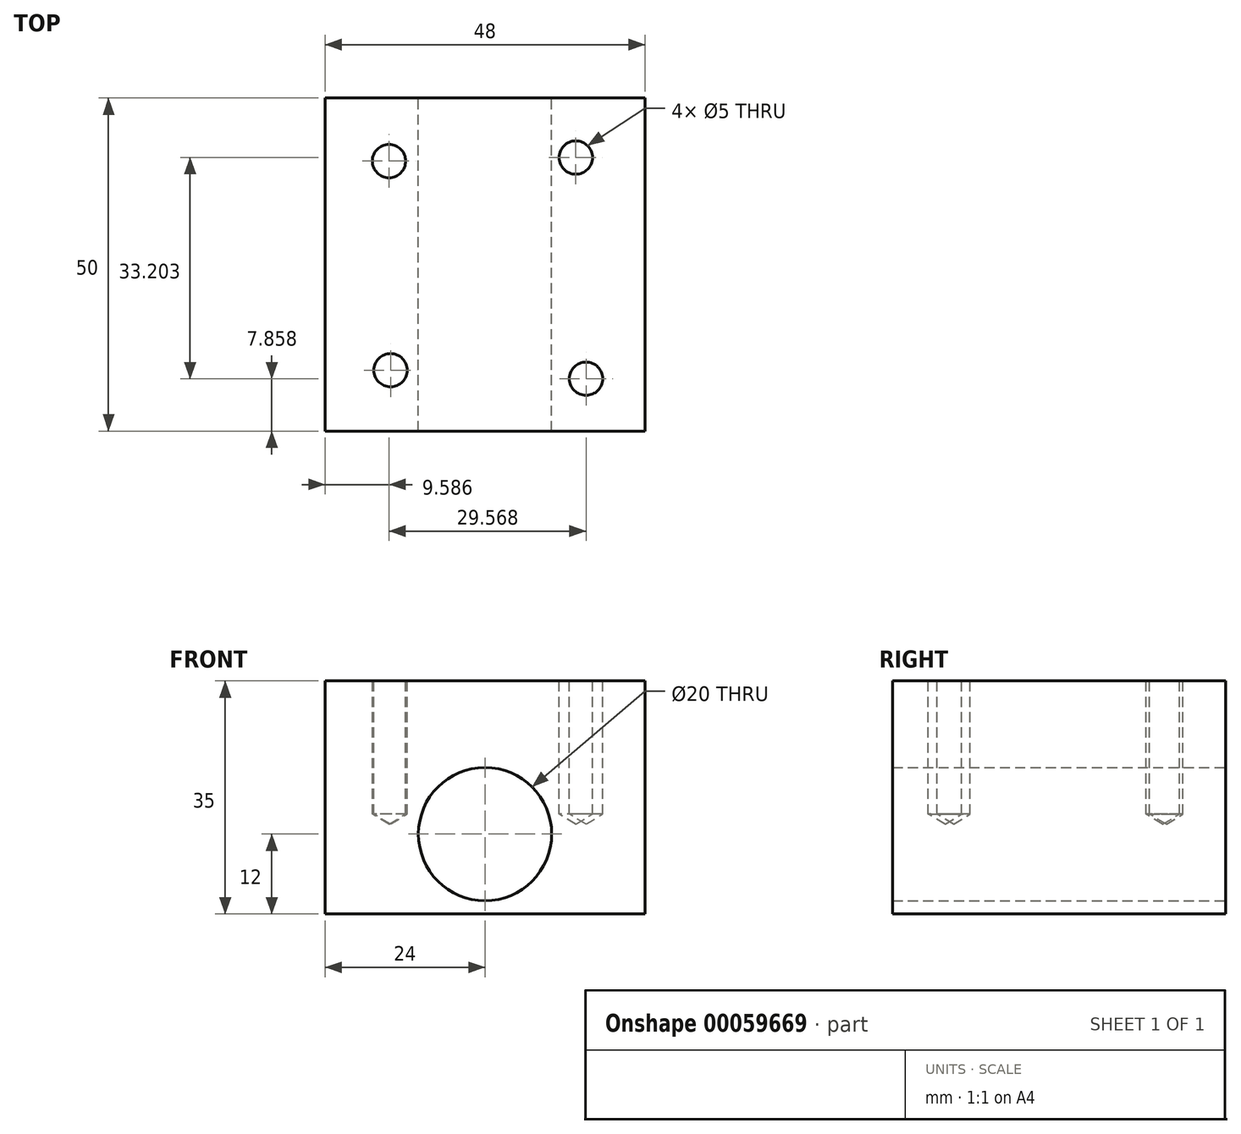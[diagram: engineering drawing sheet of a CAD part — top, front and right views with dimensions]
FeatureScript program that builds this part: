
annotation { "Feature Type Name" : "Feature", "Feature Type Description" : "" }
export const myFeature = defineFeature(function(context is Context, id is Id, definition is map)
    precondition{}
    {
        {
            var Q0;
            Q0=qCreatedBy(makeId("Front.planeOp"),FACE);
            var sketch = newSketch(context, id + "F0", { "sketchPlane" : qUnion([Q0])});
            skLineSegment(sketch, "E0.rect.bottom", {"start": v(24, 17.5) * mm, "end": v(-24, 17.5) * mm});
            skLineSegment(sketch, "E0.rect.top", {"start": v(24, -17.5) * mm, "end": v(-24, -17.5) * mm});
            skLineSegment(sketch, "E0.rect.left", {"start": v(24, 17.5) * mm, "end": v(24, -17.5) * mm});
            skLineSegment(sketch, "E0.rect.right", {"start": v(-24, 17.5) * mm, "end": v(-24, -17.5) * mm});
            skPoint(sketch, "E0.rect.middle", {"position": v(0, 0) * mm});
            skCircle(sketch, "E1", {"center": v(0, -5.5) * mm, "radius": 10 * mm});
            skSolve(sketch);
        }
        {
            var Q0;
            Q0=makeQuery(id+"F0.imprint","IMPRINT",FACE,{"disambiguationData":[TD([[makeQuery(id+"F0.imprint","IMPRINT",EDGE,{"derivedFrom":sQuery(id+"F0.wireOp",EDGE,"E0.rect.bottom")}),1.0]])]});
            extrude(context, id + "F1", {"entities" : qUnion([Q0]), "depth" : 50 * mm});
        }
        {
            var Q0;
            Q0=makeQuery(id+"F1.opExtrude","SWEPT_FACE",FACE,{"disambiguationData":[OSD([sQuery(id+"F0.wireOp",EDGE,"E0.rect.bottom")])]});
            var sketch = newSketch(context, id + "F2", { "sketchPlane" : qUnion([Q0])});
            skPoint(sketch, "E2", {"position": v(-14.18, -40.87) * mm});
            skPoint(sketch, "E3", {"position": v(-14.41, -9.47) * mm});
            skPoint(sketch, "E4", {"position": v(13.62, -8.94) * mm});
            skPoint(sketch, "E5", {"position": v(15.15, -42.14) * mm});
            skSolve(sketch);
        }
        {
            var Q0;
            Q0=sQuery(id+"F2.wireOp",VERTEX,"E3");
            var Q1;
            Q1=sQuery(id+"F2.wireOp",VERTEX,"E4");
            var Q2;
            Q2=sQuery(id+"F2.wireOp",VERTEX,"E5");
            var Q3;
            Q3=sQuery(id+"F2.wireOp",VERTEX,"E2");
            var Q4;
            Q4=makeQuery(id+"F1.opExtrude","SWEPT_BODY",BODY,{"disambiguationData":[OSD([sQuery(id+"F0.wireOp",EDGE,"E0.rect.bottom"),sQuery(id+"F0.wireOp",EDGE,"E0.rect.top"),sQuery(id+"F0.wireOp",EDGE,"E0.rect.left"),sQuery(id+"F0.wireOp",EDGE,"E0.rect.right"),sQuery(id+"F0.wireOp",EDGE,"E1")])]});
            hole(context, id + "F3", {"style" : HoleStyle.SIMPLE, "holeDiameter" : 5 * mm, "endStyle" : HoleEndStyle.BLIND, "holeDepth" : 20 * mm, "locations" : qUnion([Q0, Q1, Q2, Q3]), "scope" : qUnion([Q4])});
        }
    });
